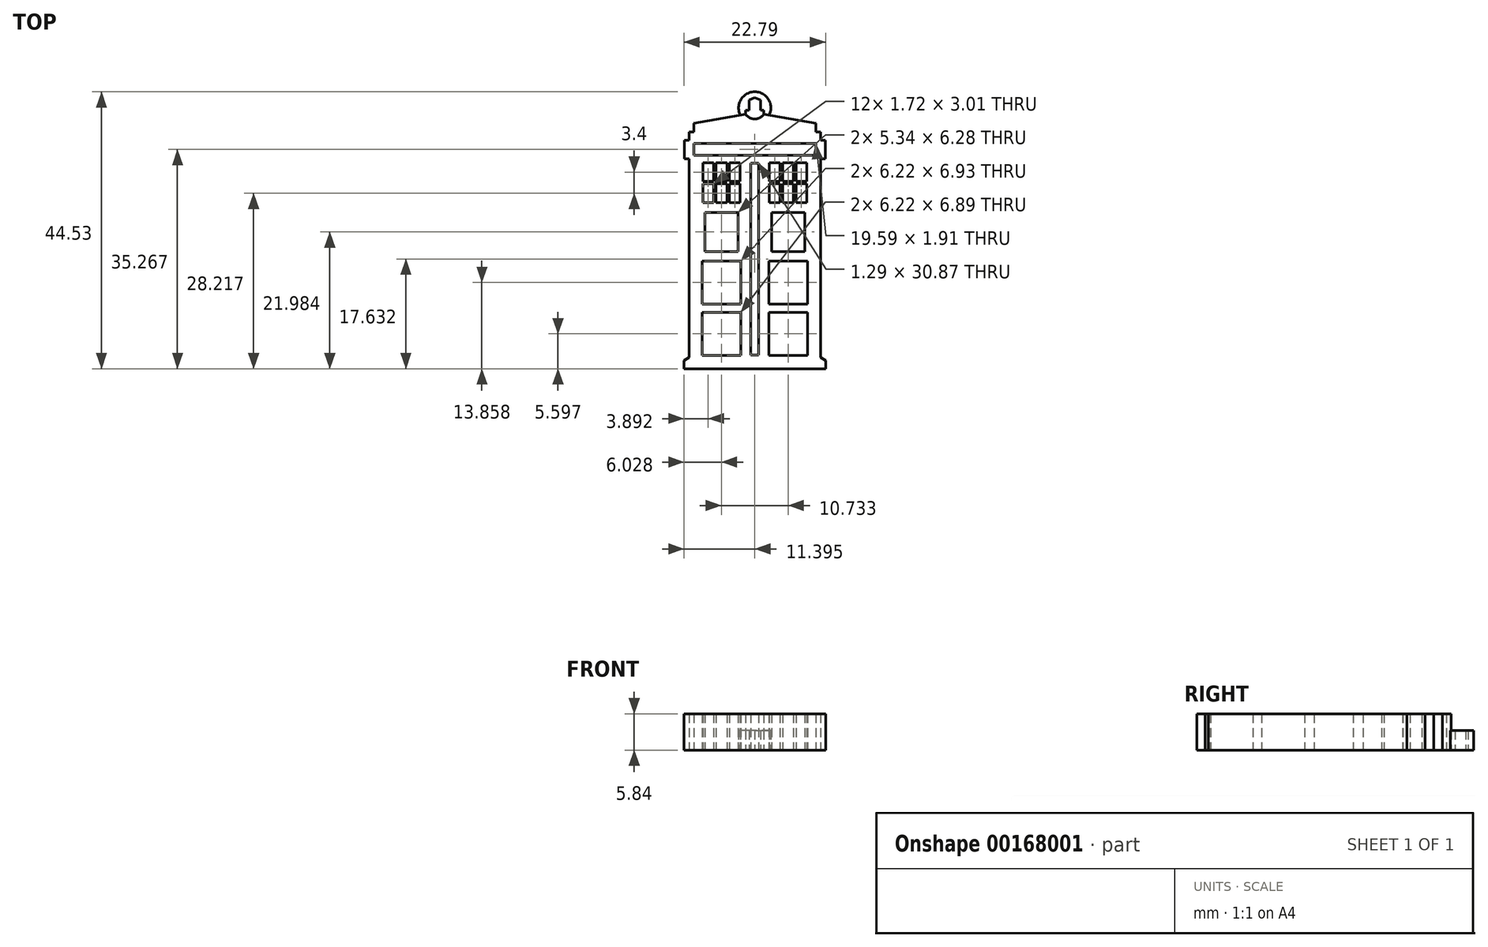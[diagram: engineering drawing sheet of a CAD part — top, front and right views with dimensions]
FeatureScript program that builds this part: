
annotation { "Feature Type Name" : "Feature", "Feature Type Description" : "" }
export const myFeature = defineFeature(function(context is Context, id is Id, definition is map)
    precondition{}
    {
        {
            var Q0;
            Q0=qCreatedBy(makeId("Top.planeOp"),FACE);
            var sketch = newSketch(context, id + "F0", { "sketchPlane" : qUnion([Q0])});
            skLineSegment(sketch, "E0", {"start": v(-4.73, 22.13) * mm, "end": v(-5.67, 21.75) * mm});
            skLineSegment(sketch, "E1", {"start": v(-5.67, 21.75) * mm, "end": v(-5.67, 20.05) * mm});
            skLineSegment(sketch, "E2", {"start": v(-5.67, 20.05) * mm, "end": v(-6.2, 20.05) * mm});
            skLineSegment(sketch, "E3", {"start": v(-6.2, 20.05) * mm, "end": v(-6.2, 19.4) * mm});
            skLineSegment(sketch, "E4", {"start": v(-6.2, 19.4) * mm, "end": v(-14.53, 18) * mm});
            skLineSegment(sketch, "E5", {"start": v(-14.53, 18) * mm, "end": v(-14.53, 16.61) * mm});
            skLineSegment(sketch, "E6", {"start": v(-14.53, 16.61) * mm, "end": v(-15.3, 16.61) * mm});
            skLineSegment(sketch, "E7", {"start": v(-15.3, 16.61) * mm, "end": v(-15.3, 15.23) * mm});
            skLineSegment(sketch, "E8", {"start": v(-15.3, 15.23) * mm, "end": v(-16.09, 15.23) * mm});
            skLineSegment(sketch, "E9", {"start": v(-16.09, 15.23) * mm, "end": v(-16.09, 12.29) * mm});
            skLineSegment(sketch, "E10", {"start": v(-16.09, 12.29) * mm, "end": v(-15.3, 12.29) * mm});
            skLineSegment(sketch, "E11", {"start": v(-15.3, 12.29) * mm, "end": v(-15.3, -19.65) * mm});
            skLineSegment(sketch, "E12", {"start": v(-15.3, -19.65) * mm, "end": v(-16.13, -20.18) * mm});
            skLineSegment(sketch, "E13", {"start": v(-16.13, -20.18) * mm, "end": v(-16.13, -21.5) * mm});
            skLineSegment(sketch, "E14", {"start": v(-16.13, -21.5) * mm, "end": v(-4.73, -21.5) * mm});
            skLineSegment(sketch, "E15", {"start": v(-4.73, 11.58) * mm, "end": v(-5.38, 11.58) * mm});
            skLineSegment(sketch, "E16", {"start": v(-5.38, 11.58) * mm, "end": v(-5.38, -19.3) * mm});
            skLineSegment(sketch, "E17", {"start": v(-5.38, -19.3) * mm, "end": v(-4.73, -19.3) * mm});
            skLineSegment(sketch, "E18.bottom", {"start": v(-12.77, 3.64) * mm, "end": v(-7.43, 3.64) * mm});
            skLineSegment(sketch, "E18.top", {"start": v(-12.77, -2.65) * mm, "end": v(-7.43, -2.65) * mm});
            skLineSegment(sketch, "E18.left", {"start": v(-12.77, 3.64) * mm, "end": v(-12.77, -2.65) * mm});
            skLineSegment(sketch, "E18.right", {"start": v(-7.43, 3.64) * mm, "end": v(-7.43, -2.65) * mm});
            skLineSegment(sketch, "E19.bottom", {"start": v(-13.21, -4.17) * mm, "end": v(-7, -4.17) * mm});
            skLineSegment(sketch, "E19.top", {"start": v(-13.21, -11.1) * mm, "end": v(-7, -11.1) * mm});
            skLineSegment(sketch, "E19.left", {"start": v(-13.21, -4.17) * mm, "end": v(-13.21, -11.1) * mm});
            skLineSegment(sketch, "E19.right", {"start": v(-7, -4.17) * mm, "end": v(-7, -11.1) * mm});
            skLineSegment(sketch, "E20.bottom", {"start": v(-13.21, -12.45) * mm, "end": v(-7, -12.45) * mm});
            skLineSegment(sketch, "E20.top", {"start": v(-13.21, -19.34) * mm, "end": v(-7, -19.34) * mm});
            skLineSegment(sketch, "E20.left", {"start": v(-13.21, -12.45) * mm, "end": v(-13.21, -19.34) * mm});
            skLineSegment(sketch, "E20.right", {"start": v(-7, -12.45) * mm, "end": v(-7, -19.34) * mm});
            skLineSegment(sketch, "E21.bottom", {"start": v(-13.1, 11.63) * mm, "end": v(-11.38, 11.63) * mm});
            skLineSegment(sketch, "E21.top", {"start": v(-13.1, 8.62) * mm, "end": v(-11.38, 8.62) * mm});
            skLineSegment(sketch, "E21.left", {"start": v(-13.1, 11.63) * mm, "end": v(-13.1, 8.62) * mm});
            skLineSegment(sketch, "E21.right", {"start": v(-11.38, 11.63) * mm, "end": v(-11.38, 8.62) * mm});
            skLineSegment(sketch, "E22.1.0.0", {"start": v(-9.23, 11.63) * mm, "end": v(-9.23, 8.62) * mm});
            skLineSegment(sketch, "E22.1.0.1", {"start": v(-10.95, 11.63) * mm, "end": v(-9.23, 11.63) * mm});
            skLineSegment(sketch, "E22.1.0.2", {"start": v(-10.95, 11.63) * mm, "end": v(-10.95, 8.62) * mm});
            skLineSegment(sketch, "E22.1.0.3", {"start": v(-10.95, 8.62) * mm, "end": v(-9.23, 8.62) * mm});
            skLineSegment(sketch, "E22.2.0.0", {"start": v(-7.08, 11.63) * mm, "end": v(-7.08, 8.62) * mm});
            skLineSegment(sketch, "E22.2.0.1", {"start": v(-8.8, 11.63) * mm, "end": v(-7.08, 11.63) * mm});
            skLineSegment(sketch, "E22.2.0.2", {"start": v(-8.8, 11.63) * mm, "end": v(-8.8, 8.62) * mm});
            skLineSegment(sketch, "E22.2.0.3", {"start": v(-8.8, 8.62) * mm, "end": v(-7.08, 8.62) * mm});
            skLineSegment(sketch, "E23.0.1.0", {"start": v(-13.1, 8.23) * mm, "end": v(-13.1, 5.22) * mm});
            skLineSegment(sketch, "E23.0.1.1", {"start": v(-13.1, 8.23) * mm, "end": v(-11.38, 8.23) * mm});
            skLineSegment(sketch, "E23.0.1.2", {"start": v(-11.38, 8.23) * mm, "end": v(-11.38, 5.22) * mm});
            skLineSegment(sketch, "E23.0.1.3", {"start": v(-13.1, 5.22) * mm, "end": v(-11.38, 5.22) * mm});
            skLineSegment(sketch, "E23.0.1.4", {"start": v(-10.95, 8.23) * mm, "end": v(-9.23, 8.23) * mm});
            skLineSegment(sketch, "E23.0.1.5", {"start": v(-10.95, 8.23) * mm, "end": v(-10.95, 5.22) * mm});
            skLineSegment(sketch, "E23.0.1.6", {"start": v(-10.95, 5.22) * mm, "end": v(-9.23, 5.22) * mm});
            skLineSegment(sketch, "E23.0.1.7", {"start": v(-9.23, 8.23) * mm, "end": v(-9.23, 5.22) * mm});
            skLineSegment(sketch, "E23.0.1.8", {"start": v(-8.8, 8.23) * mm, "end": v(-8.8, 5.22) * mm});
            skLineSegment(sketch, "E23.0.1.9", {"start": v(-7.08, 8.23) * mm, "end": v(-7.08, 5.22) * mm});
            skLineSegment(sketch, "E23.0.1.10", {"start": v(-8.8, 8.23) * mm, "end": v(-7.08, 8.23) * mm});
            skLineSegment(sketch, "E23.0.1.11", {"start": v(-8.8, 5.22) * mm, "end": v(-7.08, 5.22) * mm});
            skLineSegment(sketch, "E24.bottom", {"start": v(-4.73, 14.73) * mm, "end": v(-14.53, 14.73) * mm});
            skLineSegment(sketch, "E24.top", {"start": v(-4.73, 12.82) * mm, "end": v(-14.53, 12.82) * mm});
            skLineSegment(sketch, "E24.left", {"start": v(-4.73, 14.73) * mm, "end": v(-4.73, 12.82) * mm});
            skLineSegment(sketch, "E24.right", {"start": v(-14.53, 14.73) * mm, "end": v(-14.53, 12.82) * mm});
            skLineSegment(sketch, "E25.MirrorCS", {"start": v(-4.73, 22.13) * mm, "end": v(-3.8, 21.75) * mm});
            skLineSegment(sketch, "E26.MirrorCS", {"start": v(-3.8, 21.75) * mm, "end": v(-3.8, 20.05) * mm});
            skLineSegment(sketch, "E27.MirrorCS", {"start": v(-3.8, 20.05) * mm, "end": v(-3.28, 20.05) * mm});
            skLineSegment(sketch, "E28.MirrorCS", {"start": v(-3.28, 20.05) * mm, "end": v(-3.28, 19.4) * mm});
            skLineSegment(sketch, "E29.MirrorCS", {"start": v(-3.28, 19.4) * mm, "end": v(5.06, 18) * mm});
            skLineSegment(sketch, "E30.MirrorCS", {"start": v(5.06, 18) * mm, "end": v(5.06, 16.61) * mm});
            skLineSegment(sketch, "E31.MirrorCS", {"start": v(5.06, 16.61) * mm, "end": v(5.83, 16.61) * mm});
            skLineSegment(sketch, "E32.MirrorCS", {"start": v(5.83, 16.61) * mm, "end": v(5.83, 15.23) * mm});
            skLineSegment(sketch, "E33.MirrorCS", {"start": v(6.62, 15.23) * mm, "end": v(6.62, 12.29) * mm});
            skLineSegment(sketch, "E34.MirrorCS", {"start": v(5.83, 15.23) * mm, "end": v(6.62, 15.23) * mm});
            skLineSegment(sketch, "E35.MirrorCS", {"start": v(6.62, 12.29) * mm, "end": v(5.83, 12.29) * mm});
            skLineSegment(sketch, "E36.MirrorCS", {"start": v(-4.73, 14.73) * mm, "end": v(5.06, 14.73) * mm});
            skLineSegment(sketch, "E37.MirrorCS", {"start": v(-4.73, 12.82) * mm, "end": v(5.06, 12.82) * mm});
            skLineSegment(sketch, "E38.MirrorCS", {"start": v(5.06, 14.73) * mm, "end": v(5.06, 12.82) * mm});
            skLineSegment(sketch, "E39.MirrorCS", {"start": v(5.83, 12.29) * mm, "end": v(5.83, -19.65) * mm});
            skLineSegment(sketch, "E40.MirrorCS", {"start": v(3.63, 11.63) * mm, "end": v(1.9, 11.63) * mm});
            skLineSegment(sketch, "E41.MirrorCS", {"start": v(3.63, 11.63) * mm, "end": v(3.63, 8.62) * mm});
            skLineSegment(sketch, "E42.MirrorCS", {"start": v(3.63, 8.62) * mm, "end": v(1.9, 8.62) * mm});
            skLineSegment(sketch, "E43.MirrorCS", {"start": v(1.9, 11.63) * mm, "end": v(1.9, 8.62) * mm});
            skLineSegment(sketch, "E44.MirrorCS", {"start": v(1.48, 11.63) * mm, "end": v(-0.24, 11.63) * mm});
            skLineSegment(sketch, "E45.MirrorCS", {"start": v(1.48, 11.63) * mm, "end": v(1.48, 8.62) * mm});
            skLineSegment(sketch, "E46.MirrorCS", {"start": v(1.48, 8.62) * mm, "end": v(-0.24, 8.62) * mm});
            skLineSegment(sketch, "E47.MirrorCS", {"start": v(-0.24, 11.63) * mm, "end": v(-0.24, 8.62) * mm});
            skLineSegment(sketch, "E48.MirrorCS", {"start": v(-0.67, 11.63) * mm, "end": v(-2.4, 11.63) * mm});
            skLineSegment(sketch, "E49.MirrorCS", {"start": v(-0.67, 11.63) * mm, "end": v(-0.67, 8.62) * mm});
            skLineSegment(sketch, "E50.MirrorCS", {"start": v(-2.4, 11.63) * mm, "end": v(-2.4, 8.62) * mm});
            skLineSegment(sketch, "E51.MirrorCS", {"start": v(-0.67, 8.62) * mm, "end": v(-2.4, 8.62) * mm});
            skLineSegment(sketch, "E52.MirrorCS", {"start": v(-0.67, 8.23) * mm, "end": v(-2.4, 8.23) * mm});
            skLineSegment(sketch, "E53.MirrorCS", {"start": v(-0.67, 8.23) * mm, "end": v(-0.67, 5.22) * mm});
            skLineSegment(sketch, "E54.MirrorCS", {"start": v(-0.67, 5.22) * mm, "end": v(-2.4, 5.22) * mm});
            skLineSegment(sketch, "E55.MirrorCS", {"start": v(-2.4, 8.23) * mm, "end": v(-2.4, 5.22) * mm});
            skLineSegment(sketch, "E56.MirrorCS", {"start": v(1.48, 8.23) * mm, "end": v(-0.24, 8.23) * mm});
            skLineSegment(sketch, "E57.MirrorCS", {"start": v(1.48, 8.23) * mm, "end": v(1.48, 5.22) * mm});
            skLineSegment(sketch, "E58.MirrorCS", {"start": v(-0.24, 8.23) * mm, "end": v(-0.24, 5.22) * mm});
            skLineSegment(sketch, "E59.MirrorCS", {"start": v(1.48, 5.22) * mm, "end": v(-0.24, 5.22) * mm});
            skLineSegment(sketch, "E60.MirrorCS", {"start": v(3.63, 8.23) * mm, "end": v(3.63, 5.22) * mm});
            skLineSegment(sketch, "E61.MirrorCS", {"start": v(3.63, 8.23) * mm, "end": v(1.9, 8.23) * mm});
            skLineSegment(sketch, "E62.MirrorCS", {"start": v(1.9, 8.23) * mm, "end": v(1.9, 5.22) * mm});
            skLineSegment(sketch, "E63.MirrorCS", {"start": v(3.63, 5.22) * mm, "end": v(1.9, 5.22) * mm});
            skLineSegment(sketch, "E64.MirrorCS", {"start": v(-2.48, -12.45) * mm, "end": v(-2.48, -19.34) * mm});
            skLineSegment(sketch, "E65.MirrorCS", {"start": v(3.74, -12.45) * mm, "end": v(3.74, -19.34) * mm});
            skLineSegment(sketch, "E66.MirrorCS", {"start": v(3.74, -19.34) * mm, "end": v(-2.48, -19.34) * mm});
            skLineSegment(sketch, "E67.MirrorCS", {"start": v(3.74, -11.1) * mm, "end": v(-2.48, -11.1) * mm});
            skLineSegment(sketch, "E68.MirrorCS", {"start": v(3.74, -12.45) * mm, "end": v(-2.48, -12.45) * mm});
            skLineSegment(sketch, "E69.MirrorCS", {"start": v(6.66, -21.5) * mm, "end": v(-4.73, -21.5) * mm});
            skLineSegment(sketch, "E70.MirrorCS", {"start": v(6.66, -20.18) * mm, "end": v(6.66, -21.5) * mm});
            skLineSegment(sketch, "E71.MirrorCS", {"start": v(5.83, -19.65) * mm, "end": v(6.66, -20.18) * mm});
            skLineSegment(sketch, "E72.MirrorCS", {"start": v(-4.1, 11.58) * mm, "end": v(-4.1, -19.3) * mm});
            skLineSegment(sketch, "E73.MirrorCS", {"start": v(-4.1, -19.3) * mm, "end": v(-4.73, -19.3) * mm});
            skLineSegment(sketch, "E74.MirrorCS", {"start": v(-4.73, 11.58) * mm, "end": v(-4.1, 11.58) * mm});
            skCircle(sketch, "E75", {"center": v(-4.73, 20.44) * mm, "radius": 2.6 * mm});
            skArc(sketch, "E76", {"start": v(-6.2, 19.4) * mm, "mid": v(-4.73, 18.66) * mm, "end": v(-3.28, 19.4) * mm});
            skLineSegment(sketch, "E77.MirrorCS", {"start": v(3.3, 3.64) * mm, "end": v(-2.04, 3.64) * mm});
            skLineSegment(sketch, "E78.MirrorCS", {"start": v(-2.04, 3.64) * mm, "end": v(-2.04, -2.65) * mm});
            skLineSegment(sketch, "E79.MirrorCS", {"start": v(3.3, 3.64) * mm, "end": v(3.3, -2.65) * mm});
            skLineSegment(sketch, "E80.MirrorCS", {"start": v(3.3, -2.65) * mm, "end": v(-2.04, -2.65) * mm});
            skLineSegment(sketch, "E81.MirrorCS", {"start": v(3.74, -4.17) * mm, "end": v(-2.48, -4.17) * mm});
            skLineSegment(sketch, "E82.MirrorCS", {"start": v(3.74, -4.17) * mm, "end": v(3.74, -11.1) * mm});
            skLineSegment(sketch, "E83.MirrorCS", {"start": v(-2.48, -4.17) * mm, "end": v(-2.48, -11.1) * mm});
            skSolve(sketch);
        }
        {
            var Q0;
            {var subQ0=sQuery(id+"F0.wireOp",EDGE,"E76");Q0=makeQuery(id+"F0.imprint","IMPRINT",FACE,{"disambiguationData":[TD([[makeQuery(id+"F0.imprint","IMPRINT",EDGE,{"derivedFrom":subQ0}),-1.0]])]});}
            var Q1;
            {var subQ4=sQuery(id+"F0.wireOp",EDGE,"E5");Q1=makeQuery(id+"F0.imprint","IMPRINT",FACE,{"disambiguationData":[TD([[makeQuery(id+"F0.imprint","IMPRINT",EDGE,{"derivedFrom":subQ4}),1.0]])]});}
            extrude(context, id + "F1", {"entities" : qUnion([Q0, Q1]), "depth" : 5.84 * mm});
        }
        {
            var Q0;
            Q0=makeQuery(id+"F0.imprint","IMPRINT",FACE,{"disambiguationData":[TD([[makeQuery(id+"F0.imprint","IMPRINT",EDGE,{"derivedFrom":sQuery(id+"F0.wireOp",EDGE,"E0")}),-1.0]])]});
            extrude(context, id + "F2", {"entities" : qUnion([Q0]), "operationType" : NewBodyOperationType.ADD, "depth" : 3.17 * mm});
        }
    });
